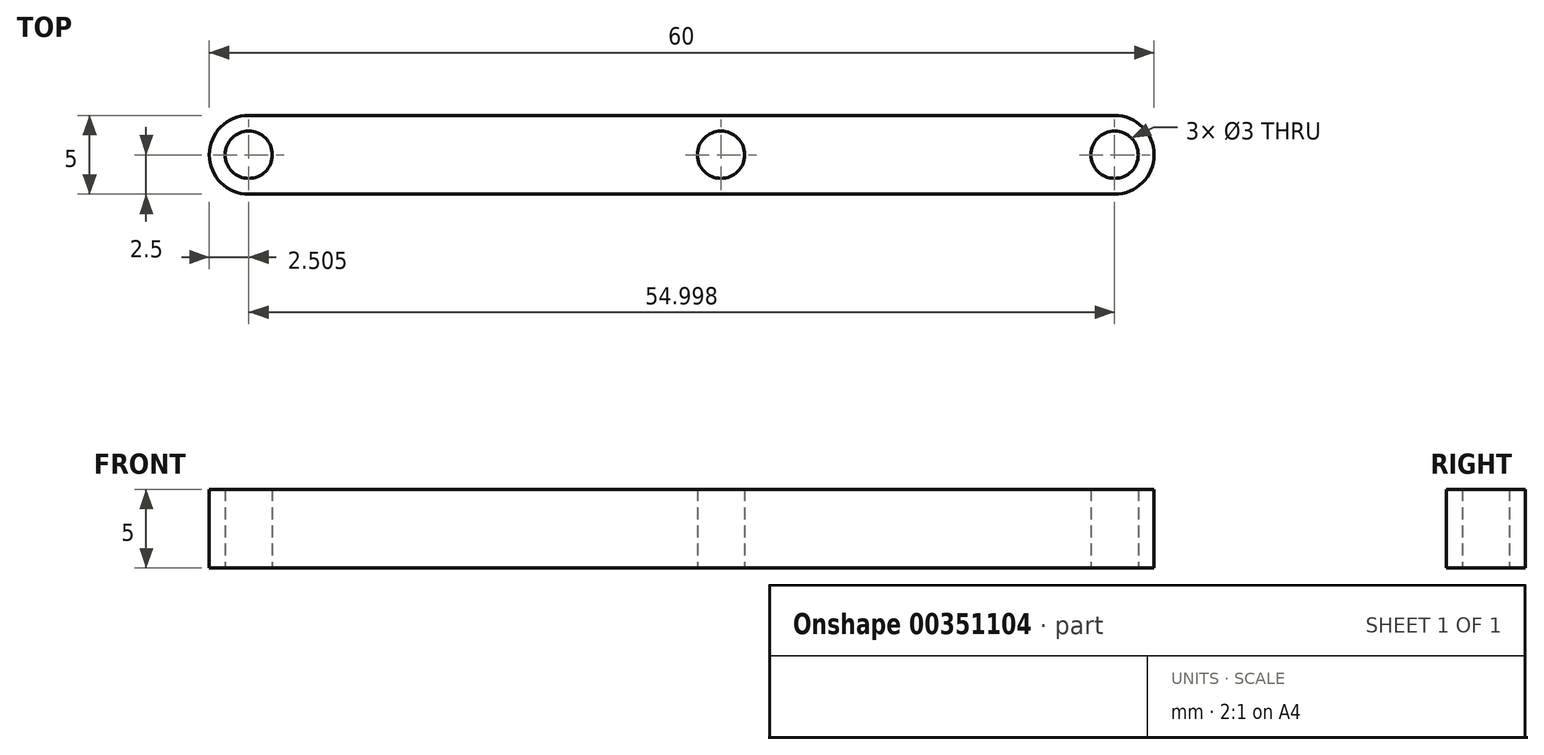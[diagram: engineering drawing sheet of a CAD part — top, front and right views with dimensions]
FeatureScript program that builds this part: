
annotation { "Feature Type Name" : "Feature", "Feature Type Description" : "" }
export const myFeature = defineFeature(function(context is Context, id is Id, definition is map)
    precondition{}
    {
        {
            var Q0;
            Q0=qCreatedBy(makeId("Top.planeOp"),FACE);
            var sketch = newSketch(context, id + "F0", { "sketchPlane" : qUnion([Q0])});
            skLineSegment(sketch, "E0.bottom", {"start": v(68.44, 0) * mm, "end": v(8.44, 0) * mm});
            skLineSegment(sketch, "E0.top", {"start": v(68.44, 5) * mm, "end": v(8.44, 5) * mm});
            skLineSegment(sketch, "E0.left", {"start": v(68.44, 0) * mm, "end": v(68.44, 5) * mm});
            skLineSegment(sketch, "E0.right", {"start": v(8.44, 0) * mm, "end": v(8.44, 5) * mm});
            skLineSegment(sketch, "E1", {"start": v(68.44, 5) * mm, "end": v(63.44, 5) * mm, "construction": true});
            skLineSegment(sketch, "E2", {"start": v(63.44, 5) * mm, "end": v(63.44, 0) * mm, "construction": true});
            skLineSegment(sketch, "E3", {"start": v(63.44, 0) * mm, "end": v(43.44, 0) * mm, "construction": true});
            skLineSegment(sketch, "E4", {"start": v(43.44, 0) * mm, "end": v(43.44, 5) * mm, "construction": true});
            skLineSegment(sketch, "E5", {"start": v(43.44, 5) * mm, "end": v(38.44, 5) * mm, "construction": true});
            skLineSegment(sketch, "E6", {"start": v(38.44, 5) * mm, "end": v(38.44, 0) * mm, "construction": true});
            skLineSegment(sketch, "E7", {"start": v(38.44, 0) * mm, "end": v(13.44, 0) * mm, "construction": true});
            skLineSegment(sketch, "E8", {"start": v(13.44, 0) * mm, "end": v(13.44, 5) * mm, "construction": true});
            skLineSegment(sketch, "E9", {"start": v(8.44, 2.5) * mm, "end": v(68.44, 2.5) * mm, "construction": true});
            skLineSegment(sketch, "E10", {"start": v(43.44, 0) * mm, "end": v(40.94, 0) * mm});
            skLineSegment(sketch, "E11", {"start": v(40.94, 0) * mm, "end": v(40.94, 5) * mm, "construction": true});
            skLineSegment(sketch, "E12", {"start": v(68.44, 5) * mm, "end": v(65.94, 5) * mm, "construction": true});
            skLineSegment(sketch, "E13", {"start": v(65.94, 5) * mm, "end": v(65.94, 0) * mm, "construction": true});
            skLineSegment(sketch, "E14", {"start": v(8.44, 5) * mm, "end": v(10.94, 5) * mm, "construction": true});
            skLineSegment(sketch, "E15", {"start": v(10.94, 5) * mm, "end": v(10.94, 0) * mm, "construction": true});
            skPoint(sketch, "E16", {"position": v(10.94, 2.5) * mm});
            skPoint(sketch, "E17", {"position": v(40.94, 2.5) * mm});
            skPoint(sketch, "E18", {"position": v(65.94, 2.5) * mm});
            skSolve(sketch);
        }
        {
            var Q0;
            Q0=makeQuery(id+"F0.imprint","IMPRINT",FACE,{"disambiguationData":[TD([[makeQuery(id+"F0.imprint","IMPRINT",EDGE,{"derivedFrom":sQuery(id+"F0.wireOp",EDGE,"E0.bottom")}),-1.0]])]});
            extrude(context, id + "F1", {"entities" : qUnion([Q0]), "depth" : 5 * mm});
        }
        {
            var Q0;
            Q0=sQuery(id+"F0.wireOp",VERTEX,"E17");
            var Q1;
            Q1=sQuery(id+"F0.wireOp",VERTEX,"E18");
            var Q2;
            Q2=sQuery(id+"F0.wireOp",VERTEX,"E16");
            var Q3;
            Q3=makeQuery(id+"F1.opExtrude","SWEPT_BODY",BODY,{"disambiguationData":[OSD([sQuery(id+"F0.wireOp",EDGE,"E0.bottom"),sQuery(id+"F0.wireOp",EDGE,"E0.top"),sQuery(id+"F0.wireOp",EDGE,"E0.left"),sQuery(id+"F0.wireOp",EDGE,"E0.right"),sQuery(id+"F0.wireOp",EDGE,"E10")])]});
            hole(context, id + "F2", {"style" : HoleStyle.SIMPLE, "endStyle" : HoleEndStyle.THROUGH, "oppositeDirection" : true, "holeDiameter" : 3 * mm, "isTappedThrough" : true, "tappedDepth" : 12 * mm, "tapClearance" : 3, "locations" : qUnion([Q0, Q1, Q2]), "scope" : qUnion([Q3])});
        }
        {
            var Q0;
            Q0=makeQuery(id+"F1.opExtrude","SWEPT_EDGE",EDGE,{"disambiguationData":[OSD([sQuery(id+"F0.wireOp",EDGE,"E0.bottom"),sQuery(id+"F0.wireOp",EDGE,"E0.right")])]});
            var Q1;
            Q1=makeQuery(id+"F1.opExtrude","SWEPT_EDGE",EDGE,{"disambiguationData":[OSD([sQuery(id+"F0.wireOp",EDGE,"E0.top"),sQuery(id+"F0.wireOp",EDGE,"E0.right")])]});
            var Q2;
            Q2=makeQuery(id+"F1.opExtrude","SWEPT_EDGE",EDGE,{"disambiguationData":[OSD([sQuery(id+"F0.wireOp",EDGE,"E0.bottom"),sQuery(id+"F0.wireOp",EDGE,"E0.left")])]});
            var Q3;
            Q3=makeQuery(id+"F1.opExtrude","SWEPT_EDGE",EDGE,{"disambiguationData":[OSD([sQuery(id+"F0.wireOp",EDGE,"E0.top"),sQuery(id+"F0.wireOp",EDGE,"E0.left")])]});
            fillet(context, id + "F3", {"entities" : qUnion([Q0, Q1, Q2, Q3]), "radius" : 2.5 * mm, "tangentPropagation" : true, "allowEdgeOverflow" : false});
        }
    });
